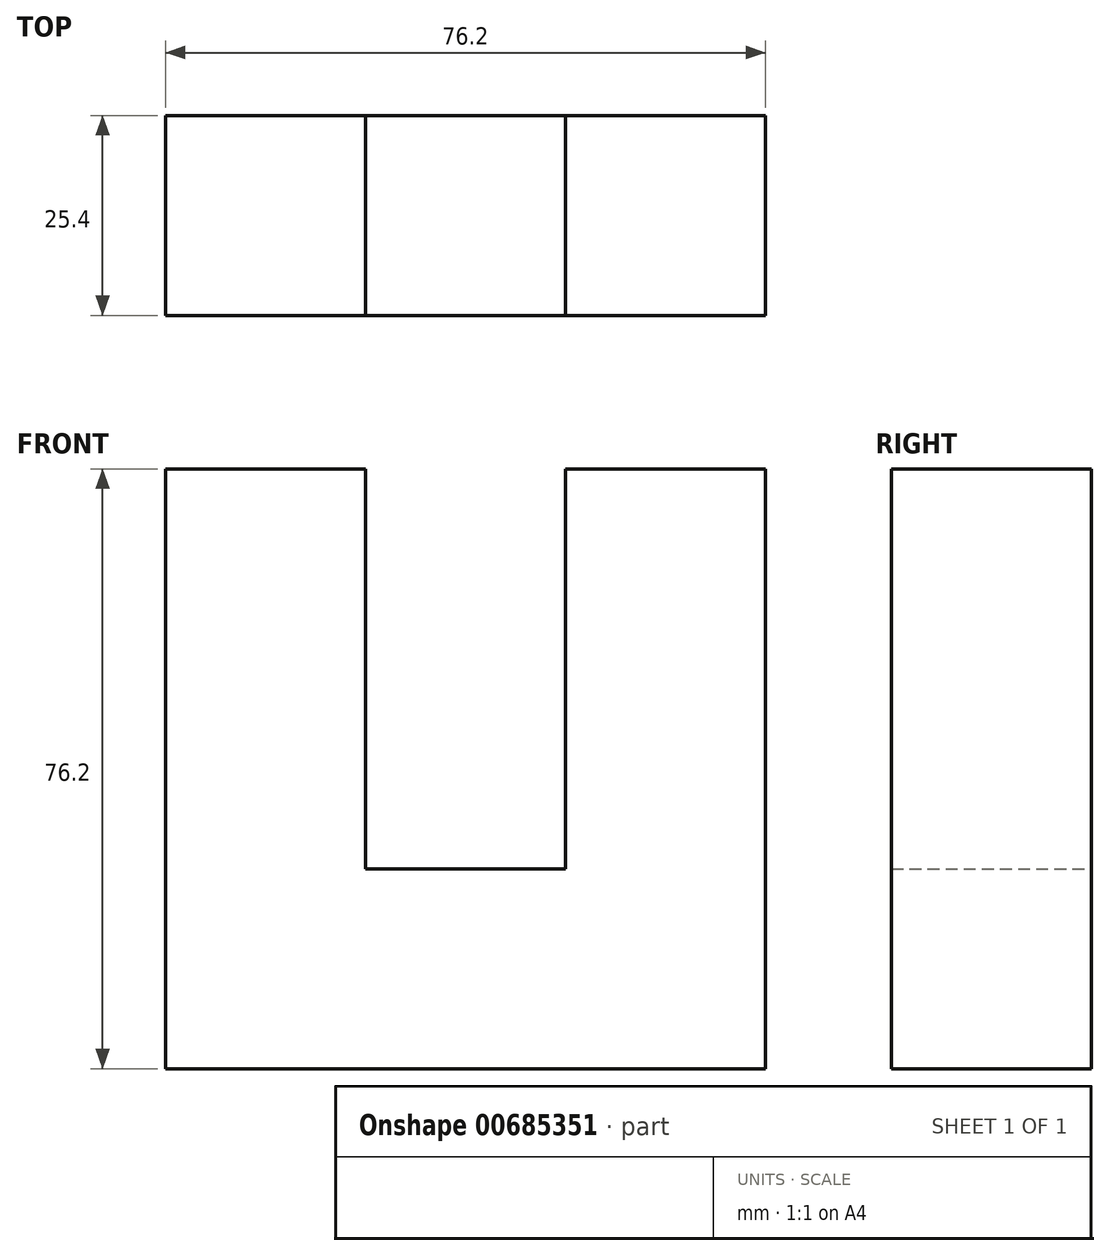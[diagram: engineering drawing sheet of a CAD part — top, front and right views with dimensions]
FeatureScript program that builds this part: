
annotation { "Feature Type Name" : "Feature", "Feature Type Description" : "" }
export const myFeature = defineFeature(function(context is Context, id is Id, definition is map)
    precondition{}
    {
        {
            var Q0;
            Q0=qCreatedBy(makeId("Front.planeOp"),FACE);
            var sketch = newSketch(context, id + "F0", { "sketchPlane" : qUnion([Q0])});
            skLineSegment(sketch, "E0", {"start": v(-25.4, 44.13) * mm, "end": v(-25.4, -32.07) * mm});
            skLineSegment(sketch, "E1", {"start": v(-25.4, 44.13) * mm, "end": v(0, 44.13) * mm});
            skLineSegment(sketch, "E2", {"start": v(0, 44.13) * mm, "end": v(0, -6.67) * mm});
            skLineSegment(sketch, "E3", {"start": v(0, -6.67) * mm, "end": v(25.4, -6.67) * mm});
            skLineSegment(sketch, "E4", {"start": v(25.4, -6.67) * mm, "end": v(25.4, 44.13) * mm});
            skLineSegment(sketch, "E5", {"start": v(25.4, 44.13) * mm, "end": v(50.8, 44.13) * mm});
            skLineSegment(sketch, "E6", {"start": v(50.8, 44.13) * mm, "end": v(50.8, -32.07) * mm});
            skLineSegment(sketch, "E7", {"start": v(-25.4, -32.07) * mm, "end": v(50.8, -32.07) * mm});
            skSolve(sketch);
        }
        {
            var Q0;
            Q0=makeQuery(id+"F0.imprint","IMPRINT",FACE,{"disambiguationData":[TD([[makeQuery(id+"F0.imprint","IMPRINT",EDGE,{"derivedFrom":sQuery(id+"F0.wireOp",EDGE,"E0")}),1.0]])]});
            extrude(context, id + "F1", {"entities" : qUnion([Q0]), "depth" : 25.4 * mm, "offsetDistance" : 25.4 * mm});
        }
    });
